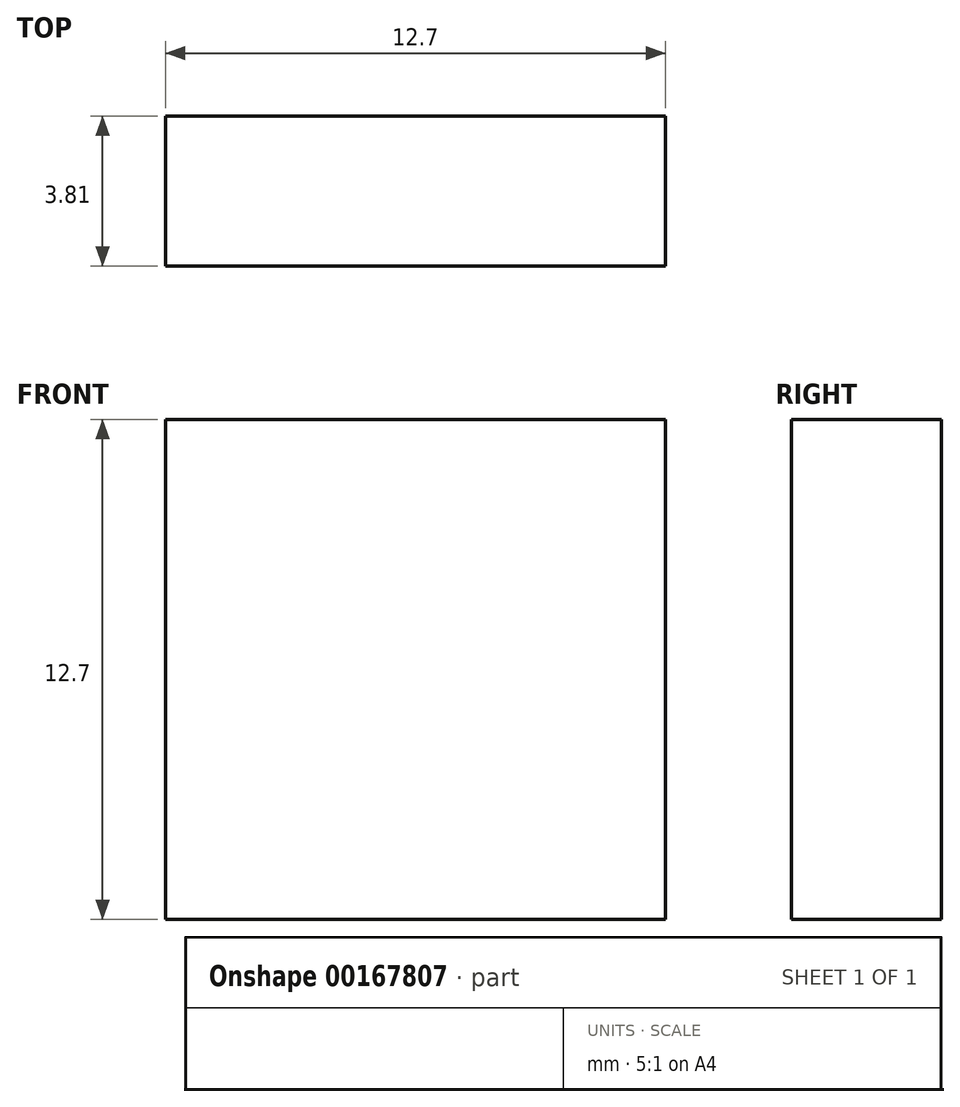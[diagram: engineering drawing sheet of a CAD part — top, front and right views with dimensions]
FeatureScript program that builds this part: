
annotation { "Feature Type Name" : "Feature", "Feature Type Description" : "" }
export const myFeature = defineFeature(function(context is Context, id is Id, definition is map)
    precondition{}
    {
        {
            var Q0;
            Q0=qCreatedBy(makeId("Top.planeOp"),FACE);
            var sketch = newSketch(context, id + "F0", { "sketchPlane" : qUnion([Q0])});
            skLineSegment(sketch, "E0.bottom", {"start": v(-67.86, 23.85) * mm, "end": v(-55.16, 23.85) * mm});
            skLineSegment(sketch, "E0.top", {"start": v(-67.86, 20.04) * mm, "end": v(-55.16, 20.04) * mm});
            skLineSegment(sketch, "E0.left", {"start": v(-67.86, 23.85) * mm, "end": v(-67.86, 20.04) * mm});
            skLineSegment(sketch, "E0.right", {"start": v(-55.16, 23.85) * mm, "end": v(-55.16, 20.04) * mm});
            skSolve(sketch);
        }
        {
            var Q0;
            Q0=makeQuery(id+"F0.imprint","IMPRINT",FACE,{"disambiguationData":[TD([[makeQuery(id+"F0.imprint","IMPRINT",EDGE,{"derivedFrom":sQuery(id+"F0.wireOp",EDGE,"E0.bottom")}),-1.0]])]});
            extrude(context, id + "F1", {"entities" : qUnion([Q0]), "depth" : 12.7 * mm});
        }
    });
